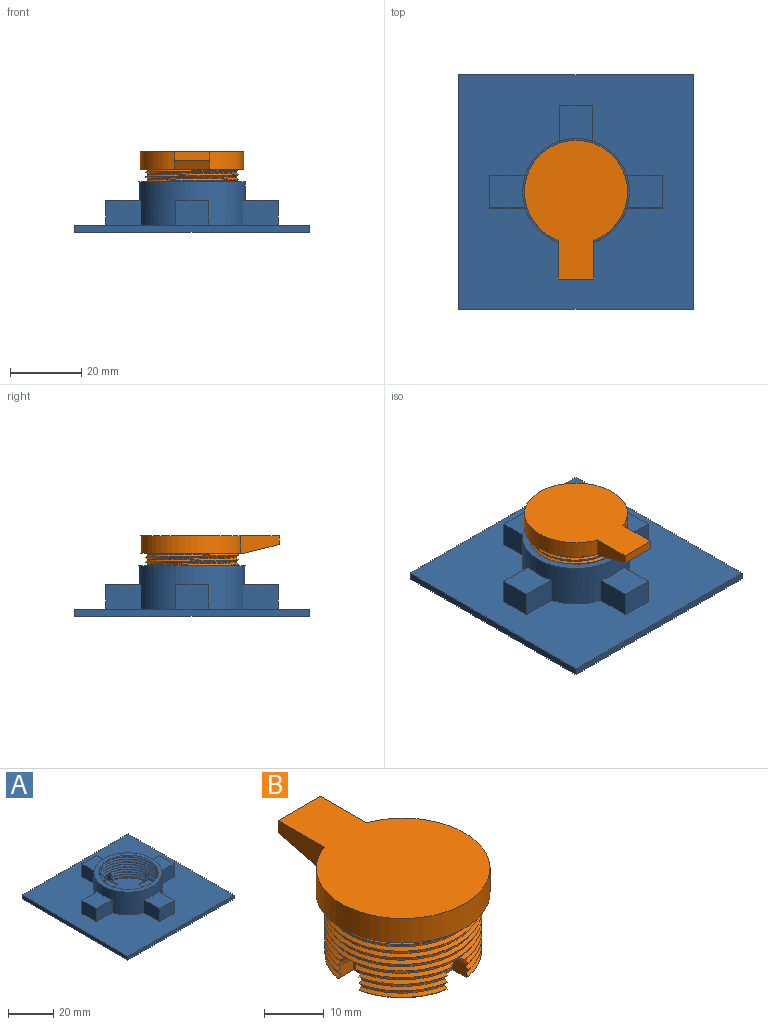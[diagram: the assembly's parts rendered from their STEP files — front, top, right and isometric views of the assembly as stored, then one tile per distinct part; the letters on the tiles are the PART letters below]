
ASSEMBLY  parts=2 mates=1
PART A: 101 faces, bbox 66.7x66.7x15.6 mm
  f0: bspline ~26.7x26.68mm, area 428.2mm2, adj f1,f2,f6,f7,f49,f55,f67,f77
  f1: bspline ~26.68x26.67mm, area 426.8mm2, adj f0,f2,f24,f38,f49,f55,f61,f77
  f2: cylinder r=12.7mm len=25.4mm, axis (0,0,1), area 15.6mm2, adj f0,f1,f49,f77
  f3: bspline ~20.03x15.43mm, area 14.7mm2, adj f5,f10,f55,f67
  f4: bspline ~20.03x15.42mm, area 14.5mm2, adj f9,f34,f49,f67
  f5: bspline ~20.03x15.42mm, area 14.3mm2, adj f3,f8,f55,f67
  f6: bspline ~20.03x15.42mm, area 15.8mm2, adj f0,f10,f55,f67
  f7: bspline ~20.03x15.43mm, area 15.2mm2, adj f0,f9,f49,f67
  f8: cylinder r=12.7mm len=9.97mm, axis (0,0,1), area 0.7mm2, adj f5,f11,f55,f67,f71
  f9: cylinder r=12.7mm len=10.35mm, axis (0,0,1), area 0.8mm2, adj f4,f7,f49,f67
  f10: cylinder r=12.7mm len=10.63mm, axis (0,0,1), area 0.8mm2, adj f3,f6,f55,f67
  f11: bspline ~20.03x15.43mm, area 14.2mm2, adj f8,f13,f55,f58,f71
  f12: bspline ~20.03x15.43mm, area 14.2mm2, adj f14,f15,f58,f71
  f13: bspline ~20.03x15.42mm, area 14.2mm2, adj f11,f15,f58,f71
  f14: bspline ~20.03x15.42mm, area 12.8mm2, adj f12,f27,f48,f58,f71
  f15: cylinder r=12.7mm len=9.95mm, axis (0,0,1), area 0.7mm2, adj f12,f13,f58,f71
  f16: bspline ~20.03x15.43mm, area 14.3mm2, adj f19,f22,f49,f61,f63
  f17: bspline ~20.03x15.43mm, area 14.2mm2, adj f20,f23,f52,f63
  f18: bspline ~20.03x15.42mm, area 15.2mm2, adj f21,f38,f55,f61
  f19: bspline ~20.03x15.42mm, area 14.2mm2, adj f16,f23,f49,f52,f63
  f20: bspline ~20.03x15.42mm, area 14.2mm2, adj f17,f26,f52,f63
  f21: bspline ~20.03x15.43mm, area 14.5mm2, adj f18,f35,f55,f61
  f22: cylinder r=12.7mm len=10.16mm, axis (0,0,1), area 0.8mm2, adj f16,f33,f49,f61
  f23: cylinder r=12.7mm len=9.95mm, axis (0,0,1), area 0.7mm2, adj f17,f19,f52,f63
  f24: cylinder r=12.7mm len=11.69mm, axis (0,0,1), area 0.9mm2, adj f1,f30,f49,f61
  f25: bspline ~20.03x15.43mm, area 12.2mm2, adj f26,f27,f47,f52,f63
  f26: cylinder r=12.7mm len=9.95mm, axis (0,0,1), area 0.7mm2, adj f20,f25,f52,f63
  f27: plane 25.85x25.84mm, normal (0,0,1), area 457.5mm2, adj f14,f25,f39,f44,f46,f47,f48,f50
  f28: bspline ~20.03x15.42mm, area 14.2mm2, adj f31,f35,f55,f59,f61,f64
  f29: bspline ~20.03x15.42mm, area 14.2mm2, adj f32,f37,f59,f64
  f30: bspline ~20.03x15.43mm, area 15.8mm2, adj f24,f33,f49,f61
  f31: bspline ~20.03x15.43mm, area 14.2mm2, adj f28,f37,f59,f64
  f32: bspline ~20.03x15.43mm, area 14.2mm2, adj f29,f40,f59,f64
  f33: bspline ~20.03x15.42mm, area 14.8mm2, adj f22,f30,f49,f61
  f34: bspline ~20.03x15.43mm, area 14.2mm2, adj f4,f36,f49,f51,f67,f70
  f35: cylinder r=12.7mm len=10.03mm, axis (0,0,1), area 0.7mm2, adj f21,f28,f55,f61
  f36: cylinder r=12.7mm len=9.95mm, axis (0,0,1), area 0.7mm2, adj f34,f41,f51,f70
  f37: cylinder r=12.7mm len=9.95mm, axis (0,0,1), area 0.7mm2, adj f29,f31,f59,f64
  f38: cylinder r=12.7mm len=11.03mm, axis (0,0,1), area 0.8mm2, adj f1,f18,f55,f61
  f39: bspline ~20.03x15.42mm, area 5mm2, adj f27,f40,f59,f64
  f40: cylinder r=12.7mm len=9.95mm, axis (0,0,1), area 0.7mm2, adj f32,f39,f59,f64
  f41: bspline ~20.03x15.42mm, area 14.2mm2, adj f36,f43,f51,f70
  f42: bspline ~20.03x15.42mm, area 14.2mm2, adj f44,f45,f51,f70
  f43: bspline ~20.03x15.43mm, area 14.2mm2, adj f41,f45,f51,f70
  f44: bspline ~20.03x15.43mm, area 5.8mm2, adj f27,f42,f51,f70
  f45: cylinder r=12.7mm len=9.95mm, axis (0,0,1), area 0.7mm2, adj f42,f43,f51,f70
  f46: bspline ~13.35x4.42mm, area 0mm2, adj f27,f48,f58
  f47: bspline ~13.35x4.42mm, area 0.1mm2, adj f25,f27,f52
  f48: cylinder r=12.7mm len=3.85mm, axis (0,0,1), area 0.1mm2, adj f14,f27,f46,f58
  f49: cylinder r=2.5mm len=9.72mm, axis (-1,0,0), area 128.5mm2, adj f0,f1,f2,f4,f7,f9,f16,f19
  f50: plane 5x0.5mm, normal (1,0,0), area 2.5mm2, adj f27,f51,f52,f53
  f51: plane 6x3mm, normal (0,-1,0), area 9.1mm2, adj f27,f34,f36,f41,f42,f43,f44,f45
  f52: plane 6x3mm, normal (0,1,0), area 9.1mm2, adj f17,f19,f20,f23,f25,f26,f27,f47
  f53: plane 6x5mm, normal (0,0,1), area 30mm2, adj f50,f51,f52,f54
  f54: plane 5x3mm, normal (-1,0,0), area 5.2mm2, adj f49,f51,f52,f53
  f55: cylinder r=2.5mm len=9.75mm, axis (1,0,0), area 127.7mm2, adj f0,f1,f3,f5,f6,f8,f10,f11
  f56: plane 5x0.5mm, normal (-1,0,0), area 2.5mm2, adj f27,f58,f59,f60
  f57: plane 5x3mm, normal (1,0,0), area 5.2mm2, adj f55,f58,f59,f60
  f58: plane 6x3mm, normal (0,-1,0), area 9mm2, adj f11,f12,f13,f14,f15,f27,f46,f48
  f59: plane 6x3mm, normal (0,1,0), area 9.1mm2, adj f27,f28,f29,f31,f32,f37,f39,f40
  f60: plane 6x5mm, normal (0,0,1), area 30mm2, adj f56,f57,f58,f59
  f61: cylinder r=2.5mm len=9.74mm, axis (0,1,0), area 128.1mm2, adj f1,f16,f18,f21,f22,f24,f28,f30
  f62: plane 5x0.5mm, normal (0,-1,0), area 2.5mm2, adj f27,f63,f64,f65
  f63: plane 6x3mm, normal (-1,0,0), area 9.1mm2, adj f16,f17,f19,f20,f23,f25,f26,f27
  f64: plane 6x3mm, normal (1,0,0), area 9.1mm2, adj f27,f28,f29,f31,f32,f37,f39,f40
  f65: plane 6x5mm, normal (0,0,1), area 30mm2, adj f62,f63,f64,f66
  f66: plane 5x3mm, normal (0,1,0), area 5.2mm2, adj f61,f63,f64,f65
  f67: cylinder r=2.5mm len=9.75mm, axis (0,-1,0), area 128.1mm2, adj f0,f3,f4,f5,f6,f7,f8,f9
  f68: plane 5x0.5mm, normal (0,1,0), area 2.5mm2, adj f27,f70,f71,f72
  f69: plane 5x3mm, normal (0,-1,0), area 5.2mm2, adj f67,f70,f71,f72
  f70: plane 6x3mm, normal (-1,0,0), area 9mm2, adj f27,f34,f36,f41,f42,f43,f44,f45
  f71: plane 6x3mm, normal (1,0,0), area 9mm2, adj f8,f11,f12,f13,f14,f15,f27,f67
  f72: plane 6x5mm, normal (0,0,1), area 30mm2, adj f68,f69,f70,f71
  f73: plane 5x5mm, normal (0,-1,0), area 19.6mm2, adj f67
  f74: plane 5x5mm, normal (1,0,0), area 19.6mm2, adj f55
  f75: plane 5x5mm, normal (0,1,0), area 19.6mm2, adj f61
  f76: plane 5x5mm, normal (-1,0,0), area 19.6mm2, adj f49
  f77: plane 30.74x30.74mm, normal (0,0,1), area 174.8mm2, adj f0,f1,f2,f100
  f78: plane 66x66mm, normal (0,0,-1), area 4356mm2, adj f82,f83,f84,f85
  f79: plane 9x7mm, normal (-1,0,0), area 63mm2, adj f93,f94,f95,f96
  f80: plane 9x7mm, normal (0,-1,0), area 63mm2, adj f90,f91,f92,f96
  f81: plane 9x7mm, normal (1,0,0), area 63mm2, adj f87,f88,f89,f96
  f82: plane 66x2mm, normal (0,-1,0), area 132mm2, adj f78,f83,f85,f96
  f83: plane 66x2mm, normal (-1,0,0), area 132mm2, adj f78,f82,f84,f96
  f84: plane 66x2mm, normal (0,1,0), area 132mm2, adj f78,f83,f85,f96
  f85: plane 66x2mm, normal (1,0,0), area 132mm2, adj f78,f82,f84,f96
  f86: plane 9x7mm, normal (0,1,0), area 63mm2, adj f96,f97,f98,f99
  f87: plane 9.89x7mm, normal (0,1,0), area 69.2mm2, adj f81,f88,f96,f100
  f88: plane 9.89x9mm, normal (0,0,1), area 84.9mm2, adj f81,f87,f89,f100
  f89: plane 9.89x7mm, normal (0,-1,0), area 69.2mm2, adj f81,f88,f96,f100
  f90: plane 9.89x7mm, normal (1,0,0), area 69.2mm2, adj f80,f91,f96,f100
  f91: plane 9.89x9mm, normal (0,0,1), area 84.9mm2, adj f80,f90,f92,f100
  f92: plane 9.89x7mm, normal (-1,0,0), area 69.2mm2, adj f80,f91,f96,f100
  f93: plane 9.89x7mm, normal (0,-1,0), area 69.2mm2, adj f79,f94,f96,f100
  f94: plane 9.89x9mm, normal (0,0,1), area 84.9mm2, adj f79,f93,f95,f100
  f95: plane 9.89x7mm, normal (0,1,0), area 69.2mm2, adj f79,f94,f96,f100
  f96: plane 66x66mm, normal (0,0,1), area 3309.7mm2, adj f79,f80,f81,f82,f83,f84,f85,f86
  f97: plane 9.89x7mm, normal (-1,0,0), area 69.2mm2, adj f86,f96,f98,f100
  f98: plane 9.89x9mm, normal (0,0,1), area 84.9mm2, adj f86,f97,f99,f100
  f99: plane 9.89x7mm, normal (1,0,0), area 69.2mm2, adj f86,f96,f98,f100
  f100: cylinder r=15mm len=30mm, axis (0,0,1), area 893.9mm2, adj f77,f87,f88,f89,f90,f91,f92,f93
PART B: 72 faces, bbox 30.8x39.5x18.5 mm
  f0: cylinder r=14.5mm len=29mm, axis (0,0,1), area 404.5mm2, adj f66,f67,f70,f71
  f1: bspline ~30.3x26.24mm, area 334.6mm2, adj f2,f3,f6,f56,f64,f66
  f2: cylinder r=12.6mm len=25.2mm, axis (0,0,1), area 134.2mm2, adj f1,f3,f10,f52,f64,f66
  f3: bspline ~30.3x26.24mm, area 341.1mm2, adj f1,f2,f27,f40,f52,f56,f60,f66
  f4: bspline ~19.68x15.15mm, area 11.3mm2, adj f8,f11,f56,f64
  f5: bspline ~19.68x15.16mm, area 11.2mm2, adj f9,f38,f51,f52,f64
  f6: bspline ~19.68x15.15mm, area 12.5mm2, adj f1,f13,f56,f64
  f7: bspline ~19.68x15.16mm, area 12mm2, adj f10,f12,f52,f64
  f8: bspline ~19.68x15.16mm, area 11.5mm2, adj f4,f13,f56,f64
  f9: bspline ~19.68x15.15mm, area 11.3mm2, adj f5,f12,f52,f64
  f10: bspline ~19.68x15.15mm, area 13.1mm2, adj f2,f7,f52,f64
  f11: cylinder r=12.6mm len=9.88mm, axis (0,0,1), area 4.6mm2, adj f4,f16,f56,f64,f65
  f12: cylinder r=12.6mm len=10.35mm, axis (0,0,1), area 4.8mm2, adj f7,f9,f52,f64
  f13: cylinder r=12.6mm len=10.66mm, axis (0,0,1), area 4.9mm2, adj f6,f8,f56,f64
  f14: bspline ~19.68x15.15mm, area 11.2mm2, adj f16,f18,f55,f65
  f15: bspline ~19.68x15.15mm, area 11mm2, adj f17,f29,f49,f55,f65
  f16: bspline ~19.68x15.16mm, area 11.2mm2, adj f11,f14,f55,f56,f65
  f17: bspline ~19.68x15.16mm, area 11.2mm2, adj f15,f18,f55,f65
  f18: cylinder r=12.6mm len=9.85mm, axis (0,0,1), area 4.6mm2, adj f14,f17,f55,f65
  f19: bspline ~19.68x15.15mm, area 11.2mm2, adj f22,f26,f52,f53,f59
  f20: bspline ~19.68x15.15mm, area 11.2mm2, adj f23,f28,f53,f59
  f21: bspline ~19.68x15.16mm, area 11.4mm2, adj f24,f37,f56,f60
  f22: bspline ~19.68x15.16mm, area 11.2mm2, adj f19,f25,f52,f59,f60
  f23: bspline ~19.68x15.16mm, area 11.2mm2, adj f20,f26,f53,f59
  f24: bspline ~19.68x15.15mm, area 11.8mm2, adj f21,f40,f56,f60
  f25: cylinder r=12.6mm len=10.12mm, axis (0,0,1), area 4.7mm2, adj f22,f33,f52,f60
  f26: cylinder r=12.6mm len=9.85mm, axis (0,0,1), area 4.6mm2, adj f19,f23,f53,f59
  f27: cylinder r=12.6mm len=12.09mm, axis (0,0,1), area 5.4mm2, adj f3,f36,f52,f60
  f28: cylinder r=12.6mm len=9.85mm, axis (0,0,1), area 4.6mm2, adj f20,f30,f53,f59
  f29: plane 25.48x25.46mm, normal (0,0,-1), area 444.5mm2, adj f15,f30,f41,f43,f47,f48,f49,f50
  f30: bspline ~19.68x15.16mm, area 9.2mm2, adj f28,f29,f47,f53,f59
  f31: bspline ~19.68x15.16mm, area 11.2mm2, adj f34,f39,f57,f61
  f32: bspline ~19.68x15.16mm, area 11.2mm2, adj f35,f41,f57,f61
  f33: bspline ~19.68x15.15mm, area 11.7mm2, adj f25,f36,f52,f60
  f34: bspline ~19.68x15.15mm, area 11.2mm2, adj f31,f37,f56,f57,f60,f61
  f35: bspline ~19.68x15.15mm, area 11.2mm2, adj f32,f39,f57,f61
  f36: bspline ~19.68x15.16mm, area 12.3mm2, adj f27,f33,f52,f60
  f37: cylinder r=12.6mm len=9.97mm, axis (0,0,1), area 4.6mm2, adj f21,f34,f56,f60
  f38: cylinder r=12.6mm len=9.85mm, axis (0,0,1), area 4.6mm2, adj f5,f44,f51,f63,f64
  f39: cylinder r=12.6mm len=9.85mm, axis (0,0,1), area 4.6mm2, adj f31,f35,f57,f61
  f40: cylinder r=12.6mm len=11.14mm, axis (0,0,1), area 5.1mm2, adj f3,f24,f56,f60
  f41: cylinder r=12.6mm len=9.85mm, axis (0,0,1), area 4.6mm2, adj f29,f32,f48,f57,f61
  f42: bspline ~19.68x15.16mm, area 11.2mm2, adj f44,f46,f51,f63
  f43: bspline ~19.68x15.16mm, area 5.6mm2, adj f29,f45,f51,f63
  f44: bspline ~19.68x15.15mm, area 11.2mm2, adj f38,f42,f51,f63
  f45: bspline ~19.68x15.15mm, area 11.2mm2, adj f43,f46,f51,f63
  f46: cylinder r=12.6mm len=9.85mm, axis (0,0,1), area 4.6mm2, adj f42,f45,f51,f63
  f47: bspline ~13.12x4.33mm, area 0.1mm2, adj f29,f30,f53
  f48: bspline ~19.68x15.15mm, area 2.2mm2, adj f29,f41,f61
  f49: cylinder r=12.6mm len=8.87mm, axis (0,0,1), area 1.2mm2, adj f15,f29,f55
  f50: plane 5x5mm, normal (-1,0,0), area 22.3mm2, adj f29,f51,f52,f53
  f51: plane 3.68x2.5mm, normal (0,1,0), area 8.4mm2, adj f5,f29,f38,f42,f43,f44,f45,f46
  f52: cylinder r=2.5mm len=5mm, axis (-1,0,0), area 27mm2, adj f2,f3,f5,f7,f9,f10,f12,f19
  f53: plane 3.68x2.5mm, normal (0,-1,0), area 8.3mm2, adj f19,f20,f23,f26,f28,f29,f30,f47
  f54: plane 5x5mm, normal (1,0,0), area 22.3mm2, adj f29,f55,f56,f57
  f55: plane 3.68x2.5mm, normal (0,1,0), area 8.4mm2, adj f14,f15,f16,f17,f18,f29,f49,f54
  f56: cylinder r=2.5mm len=5mm, axis (1,0,0), area 27.6mm2, adj f1,f3,f4,f6,f8,f11,f13,f16
  f57: plane 3.68x2.5mm, normal (0,-1,0), area 8.4mm2, adj f29,f31,f32,f34,f35,f39,f41,f54
  f58: plane 5x5mm, normal (0,1,0), area 22.3mm2, adj f29,f59,f60,f61
  f59: plane 3.68x2.5mm, normal (1,0,0), area 8.3mm2, adj f19,f20,f22,f23,f26,f28,f29,f30
  f60: cylinder r=2.5mm len=5mm, axis (0,1,0), area 27.3mm2, adj f3,f21,f22,f24,f25,f27,f33,f34
  f61: plane 3.68x2.5mm, normal (-1,0,0), area 8.4mm2, adj f29,f31,f32,f34,f35,f39,f41,f48
  f62: plane 5x5mm, normal (0,-1,0), area 22.3mm2, adj f29,f63,f64,f65
  f63: plane 3.68x2.5mm, normal (1,0,0), area 8.4mm2, adj f29,f38,f42,f43,f44,f45,f46,f62
  f64: cylinder r=2.5mm len=5mm, axis (0,-1,0), area 27.3mm2, adj f1,f2,f4,f5,f6,f7,f8,f9
  f65: plane 3.68x2.5mm, normal (-1,0,0), area 8.4mm2, adj f11,f14,f15,f16,f17,f18,f29,f62
  f66: plane 29.47x29.47mm, normal (0,0,-1), area 148.6mm2, adj f0,f1,f2,f3,f69,f70,f71
  f67: plane 39x29mm, normal (0,0,1), area 763.4mm2, adj f0,f68,f70,f71
  f68: plane 10x2.5mm, normal (0,1,0), area 25mm2, adj f67,f69,f70,f71
  f69: plane 10x10mm, normal (0,0.24,-0.97), area 103.1mm2, adj f66,f68,f70,f71
  f70: plane 10.89x5mm, normal (1,0,0), area 41.9mm2, adj f0,f66,f67,f68,f69
  f71: plane 10.89x5mm, normal (-1,0,0), area 41.9mm2, adj f0,f66,f67,f68,f69
PLACE A t=(13.87,4.08,-4.31)mm fixed
PLACE B rot(axis=(0,0,1),180deg) t=(13.87,4.08,-4.31)mm
MATE cylindrical A.f2 <-> B.f2  axis (0,0,1) through (13.87,4.08,-24.31)mm
